# Revit family: e934fb6b-c4dc-425c-81c7-190449036f97_RevoPRIME_revit_template_model_3d_rfa
name_source: partatom
category: Doors
units: mm (PartAtom-declared; Revit-internal decimal feet)

## family parameters
Always vertical = Yes
Cut with Voids When Loaded = Yes
Host = Wall
OmniClass Number = 23.30.10.17.21
OmniClass Title = Revolving Doors
Room Calculation Point = No
Shared = No

## types (1)
- e934fb6b-c4dc-425c-81c7-190449036f97_RevoPRIME_revit_template_model_3d_rfa
    Analytic Construction = <None>
    Define Thermal Properties by = Schematic Type
    Description = Automatic revolving door system with low canopy height and narrow profile system for three- or four-leaf doors
    FP_3_hojas = Yes
    FP_4_hojas = No
    FP_Altura_de_canopy = 76 mm  [stored 0.249344 ft]
    FP_Altura_de_marco_RC2 = 0 mm  [stored 0 ft]
    FP_Altura_de_paso = 2324 mm  [stored 7.62467 ft]
    FP_Altura_de_puerta = 2400 mm
    FP_Altura_del_motor_empotrado_de_suelo = 101 mm  [stored 0.331365 ft]
    FP_Ancho_de_hoja = 930 mm  [stored 3.05118 ft]
    FP_Ancho_de_marco_RC2 = 0 mm  [stored 0 ft]
    FP_Ancho_de_paso_CAL = 890 mm  [stored 2.91995 ft]
    FP_Ancho_del_motor_empotrado_de_suelo = 680 mm  [stored 2.23097 ft]
    FP_Ancho_perfil_vertical_interior_hoja_móvil = 35 mm  [stored 0.114829 ft]
    FP_Compensación_medida_altura_de_canopy = 76 mm  [stored 0.249344 ft]
    FP_Detalles_de_salida_2D = No
    FP_Diámetro_de_puerta_con_cierre_nocturno = 2000 mm  [stored 6.56168 ft]
    FP_Diámetro_exterior_de_puerta = 2000 mm  [stored 6.56168 ft]
    FP_Eje_central = Yes
    FP_Longitud_del_motor_empotrado_de_suelo = 937 mm  [stored 3.07415 ft]
    FP_Material _del_Canopy = Aluminium
    FP_Material_Anillo_de_suelo = Stainless_steel
    FP_Material_de_recubrimiento_de_suelo = Rubber Black
    FP_Material_de_relleno_de_la_hoja = Glass
    FP_Material_del_marco = Aluminium
    FP_Motor_en_suelo = No
    FP_Posición_de_la_flecha = 620 mm  [stored 2.03412 ft]
    FP_Puerta_con_cierre_nocturno = No
    FP_Puerta_con_cierre_nocturno_exterior = Yes
    FP_Puerta_con_cierre_nocturno_interior = No
    FP_Puerta_sin_cierre_nocturno = Yes
    FP_Radio_externo = 1000 mm  [stored 3.28084 ft]
    FP_Radio_interno = 960 mm  [stored 3.14961 ft]
    FP_Techo_de_cristal = No
    FP_Ángulo = 60.00°
    Function = Exterior
    GEZEIDBIM = 141742
    Height = 2324 mm  [stored 7.62467 ft]
    Manufacturer = GEZE GmbH
    Model = Revo.PRIME
    Nombre_del_producto = Revo.PRIME
    Operation = REVOLVING
    Rough Height = 2400 mm
    Rough Width = 2000 mm  [stored 6.56168 ft]
    SP_Altura_de_la_cubierta_mín = 75
    SP_Altura_paso_libre = 3500
    SP_Aro_de_suelo = Si
    SP_Automatismo_de_pavimento = No
    SP_Bloqueo = Manualmente, Barra, electromecánica
    SP_Con_automatismo_de_posicionamiento_opcional = Si
    SP_Con_reductor_de_velocidad_opcional = Si
    SP_Conformidad_estándar = EN 16005
    SP_Cortina_de_aire = Cortina de aire eléctrica, Cortina de aire de agua caliente, en función de la version constructiva del techo
    SP_Disposición_cierre_nocturno = Interior, Exterior
    SP_Diámetro_interior_máx = 3800
    SP_Diámetro_interior_mín = 1800
    SP_Función_Break_out_BO = -
    SP_Función_Servo = No
    SP_GEZE_Documentos = https://pic.geze.com
    SP_Idoneidad_para_puertas_de_rutas_de_evacuación_y_emergencia = -
    SP_Iluminación = en la variante con techo
    SP_Manejo_manual = Si
    SP_Manejo_totalmente_automático = Si
    SP_Modelo_cierre_nocturno = VSG de 10 mm, Vidrio ISO de 22 mm, panel con relleno de 22 mm, vidrios especiales bajo solicitud
    SP_Para_sistemas_de_puerta_de_3_hojas = Si
    SP_Para_sistemas_de_puerta_de_4_hojas = Si
    SP_Pulsador_para_discapacitados = Si
    SP_Revestimiento_del_suelo = Entrance mat, Entrance mat according to customer wishes
    SP_Tipo_cierre_nocturno = Manualmente, Automático
    SP_Tiradores_de_la_puerta_horizontales_o_verticales = Si
    SP_Versiones_constructivas_del_techo = cobertor de chapa óptico, techo impermeable con vierteaguas
    SP_Versión_partes_laterales = VSG de 10 mm, panel con relleno de 22 mm, panel liso de 34 mm, vidrios especiales bajo solicitud
    Thickness = 30 mm  [stored 0.0984252 ft]
    URL = https://www.geze.com
    Wall Closure = By host
    Width = 2000 mm  [stored 6.56168 ft]

note: [stored X ft] marks values corroborated as IEEE doubles in the binary element streams (Revit-internal decimal feet)
